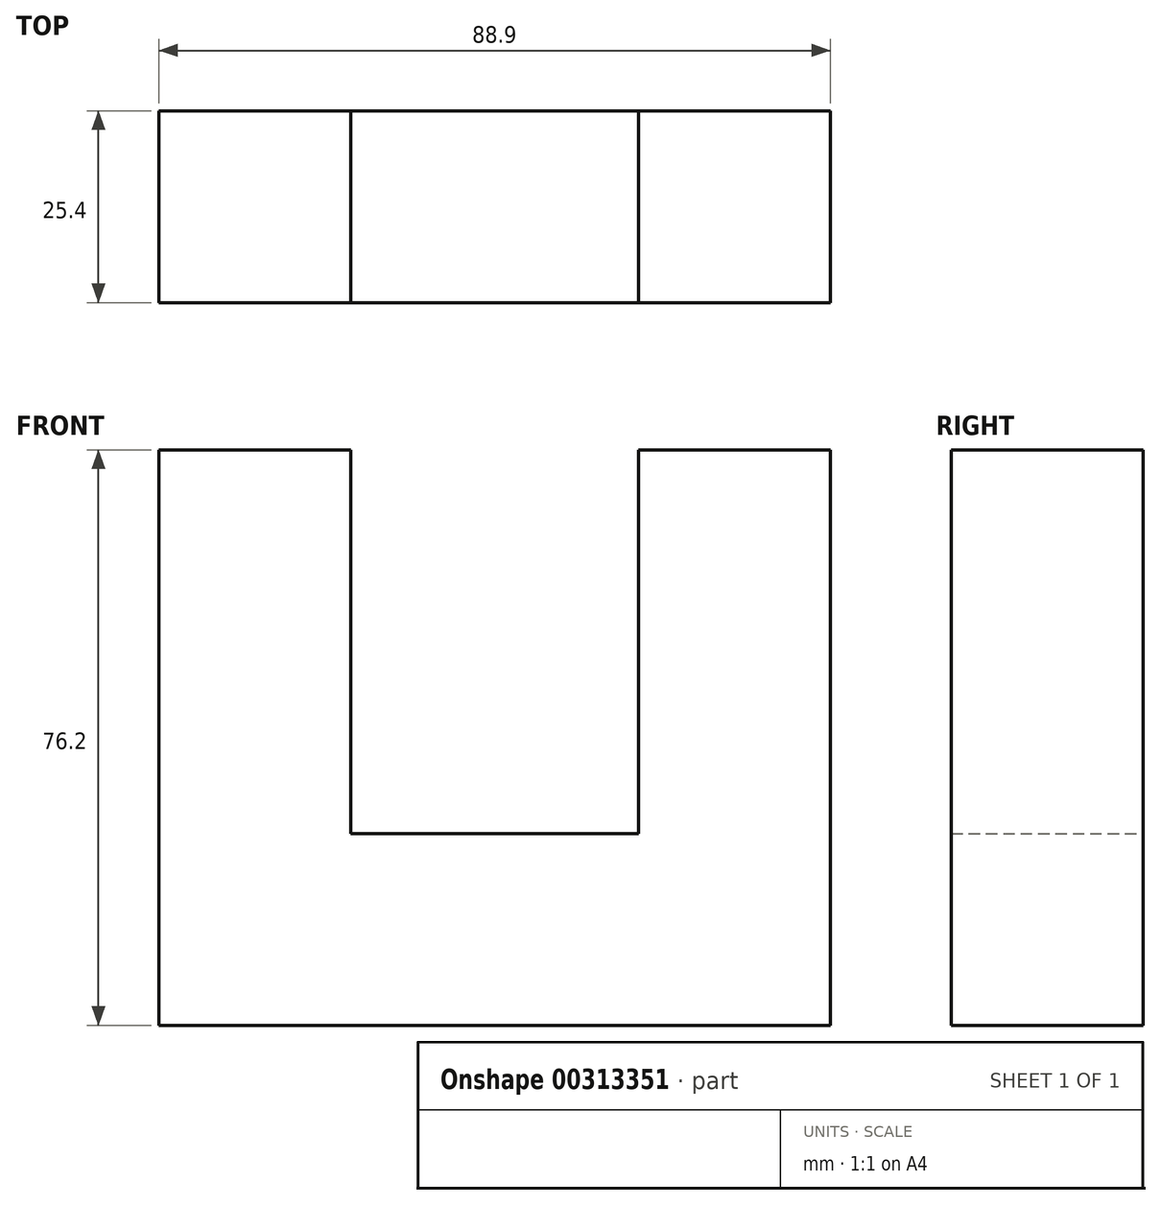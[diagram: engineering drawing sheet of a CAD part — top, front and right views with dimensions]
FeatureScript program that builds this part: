
annotation { "Feature Type Name" : "Feature", "Feature Type Description" : "" }
export const myFeature = defineFeature(function(context is Context, id is Id, definition is map)
    precondition{}
    {
        {
            var Q0;
            Q0=qCreatedBy(makeId("Front.planeOp"),FACE);
            var sketch = newSketch(context, id + "F0", { "sketchPlane" : qUnion([Q0])});
            skLineSegment(sketch, "E0", {"start": v(-47.32, -50.6) * mm, "end": v(41.58, -50.6) * mm});
            skLineSegment(sketch, "E1", {"start": v(41.58, -50.6) * mm, "end": v(41.58, 25.6) * mm});
            skLineSegment(sketch, "E2", {"start": v(41.58, 25.6) * mm, "end": v(16.18, 25.6) * mm});
            skLineSegment(sketch, "E3", {"start": v(16.18, 25.6) * mm, "end": v(16.18, -25.2) * mm});
            skLineSegment(sketch, "E4", {"start": v(16.18, -25.2) * mm, "end": v(-21.92, -25.2) * mm});
            skLineSegment(sketch, "E5", {"start": v(-21.92, -25.2) * mm, "end": v(-21.92, 25.6) * mm});
            skLineSegment(sketch, "E6", {"start": v(-21.92, 25.6) * mm, "end": v(-47.32, 25.6) * mm});
            skLineSegment(sketch, "E7", {"start": v(-47.32, 25.6) * mm, "end": v(-47.32, -50.6) * mm});
            skSolve(sketch);
        }
        {
            var Q0;
            Q0=makeQuery(id+"F0.imprint","IMPRINT",FACE,{"disambiguationData":[TD([[makeQuery(id+"F0.imprint","IMPRINT",EDGE,{"derivedFrom":sQuery(id+"F0.wireOp",EDGE,"E0")}),1.0]])]});
            extrude(context, id + "F1", {"entities" : qUnion([Q0]), "depth" : 25.4 * mm});
        }
    });
